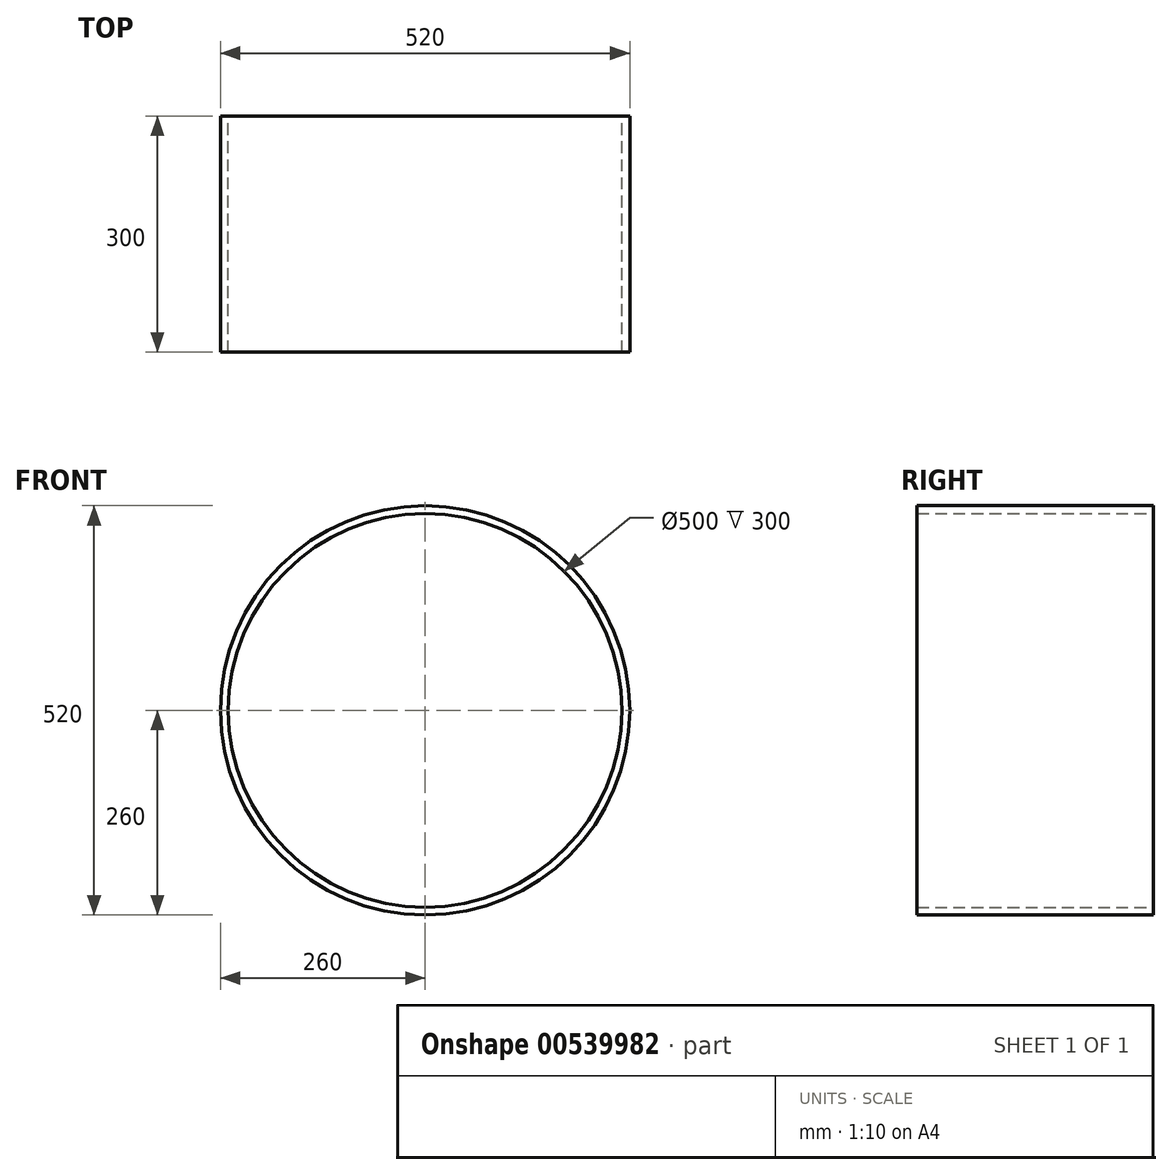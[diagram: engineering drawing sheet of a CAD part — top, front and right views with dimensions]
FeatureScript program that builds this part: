
annotation { "Feature Type Name" : "Feature", "Feature Type Description" : "" }
export const myFeature = defineFeature(function(context is Context, id is Id, definition is map)
    precondition{}
    {
        {
            var Q0;
            Q0=qCreatedBy(makeId("Front.planeOp"),FACE);
            var sketch = newSketch(context, id + "F0", { "sketchPlane" : qUnion([Q0])});
            skCircle(sketch, "E0", {"center": v(0, 0) * mm, "radius": 250 * mm});
            skCircle(sketch, "E1.0", {"center": v(0, 0) * mm, "radius": 260 * mm});
            skSolve(sketch);
        }
        {
            var Q0;
            Q0=makeQuery(id+"F0.imprint","IMPRINT",FACE,{"disambiguationData":[TD([[makeQuery(id+"F0.imprint","IMPRINT",EDGE,{"derivedFrom":sQuery(id+"F0.wireOp",EDGE,"E0")}),-1.0]])]});
            extrude(context, id + "F1", {"entities" : qUnion([Q0]), "depth" : 300 * mm, "offsetDistance" : 25 * mm});
        }
    });
